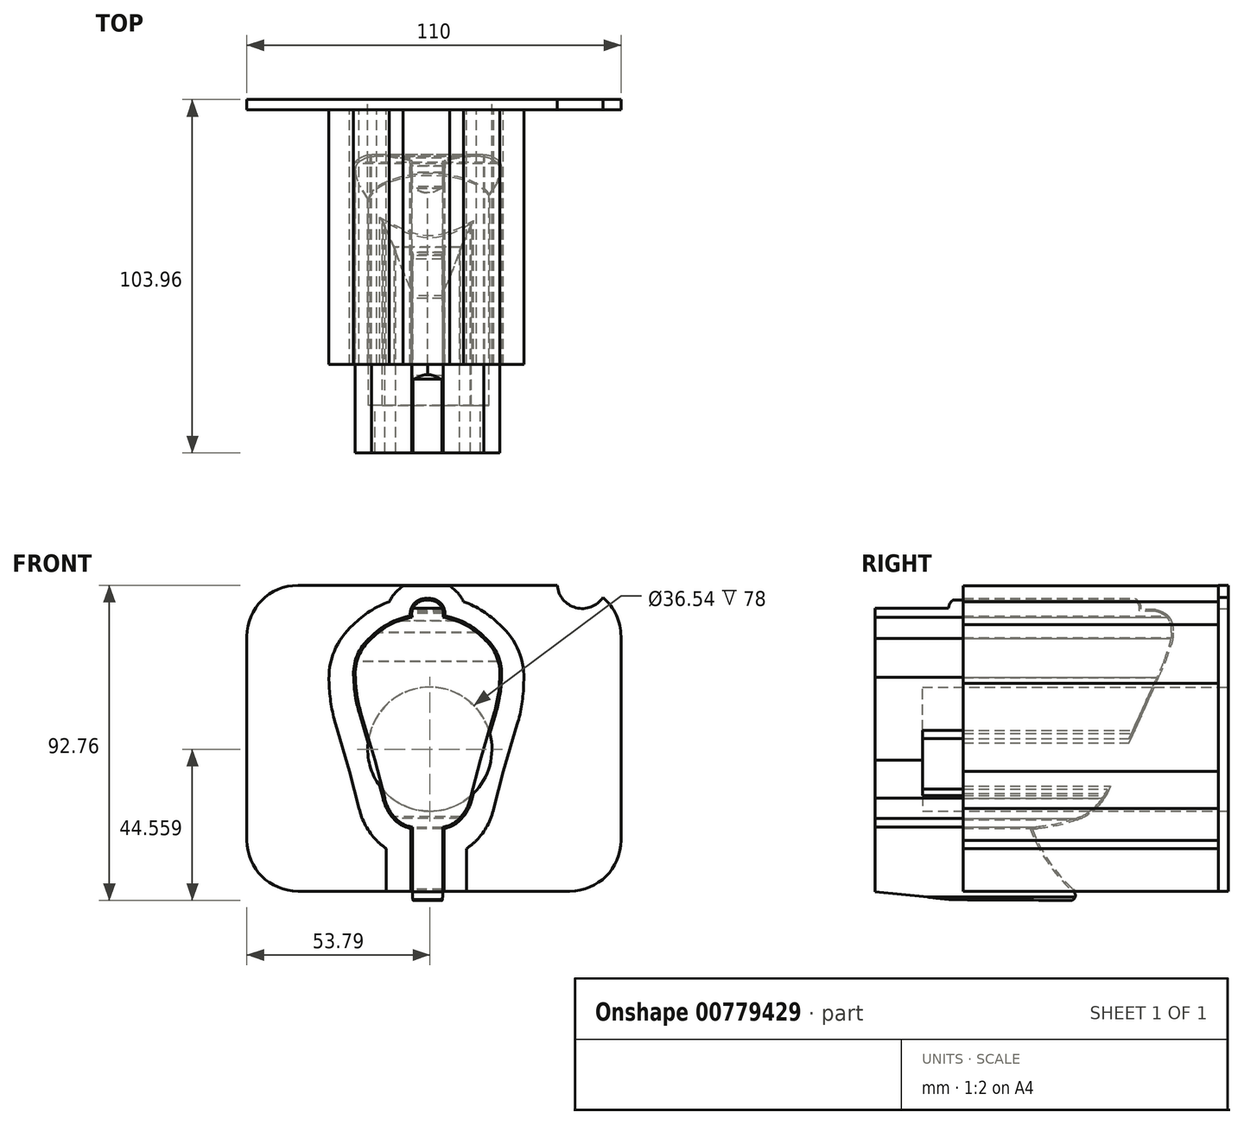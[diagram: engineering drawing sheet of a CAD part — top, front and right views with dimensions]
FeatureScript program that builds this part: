
annotation { "Feature Type Name" : "Feature", "Feature Type Description" : "" }
export const myFeature = defineFeature(function(context is Context, id is Id, definition is map)
    precondition{}
    {
        {
            var Q0;
            Q0=qCreatedBy(makeId("Front.planeOp"),FACE);
            var sketch = newSketch(context, id + "F0", { "sketchPlane" : qUnion([Q0])});
            skArc(sketch, "E0", {"start": v(0, -54.8) * mm, "mid": v(3.03, -53.66) * mm, "end": v(4.41, -50.73) * mm});
            skLineSegment(sketch, "E1", {"start": v(4.41, -50.73) * mm, "end": v(4.41, -30.1) * mm});
            skArc(sketch, "E2", {"start": v(4.41, -30.1) * mm, "mid": v(7.1, -29.25) * mm, "end": v(9.36, -27.55) * mm});
            skArc(sketch, "E3", {"start": v(9.36, -27.55) * mm, "mid": v(11.4, -24.8) * mm, "end": v(12.61, -21.6) * mm});
            skLineSegment(sketch, "E4", {"start": v(12.61, -21.6) * mm, "end": v(15.48, -10.44) * mm});
            skLineSegment(sketch, "E5", {"start": v(15.48, -10.44) * mm, "end": v(19.6, 3.52) * mm});
            skArc(sketch, "E6", {"start": v(16.49, 25.34) * mm, "mid": v(11, 29.45) * mm, "end": v(4.5, 31.58) * mm});
            skArc(sketch, "E7", {"start": v(4.5, 31.58) * mm, "mid": v(3.6, 35.3) * mm, "end": v(0, 36.62) * mm});
            skArc(sketch, "E8", {"start": v(19.6, 3.52) * mm, "mid": v(20.76, 8.66) * mm, "end": v(21.2, 13.91) * mm});
            skArc(sketch, "E9", {"start": v(21.2, 13.91) * mm, "mid": v(20.25, 20.2) * mm, "end": v(16.49, 25.34) * mm});
            skArc(sketch, "E10.MirrorCS", {"start": v(-4.5, 31.58) * mm, "mid": v(-3.6, 35.3) * mm, "end": v(0, 36.62) * mm});
            skArc(sketch, "E11.MirrorCS", {"start": v(-16.49, 25.34) * mm, "mid": v(-11, 29.45) * mm, "end": v(-4.5, 31.58) * mm});
            skArc(sketch, "E12.MirrorCS", {"start": v(-21.2, 13.91) * mm, "mid": v(-20.25, 20.2) * mm, "end": v(-16.49, 25.34) * mm});
            skArc(sketch, "E13.MirrorCS", {"start": v(-19.6, 3.52) * mm, "mid": v(-20.76, 8.66) * mm, "end": v(-21.2, 13.91) * mm});
            skLineSegment(sketch, "E14.MirrorCS", {"start": v(-15.48, -10.44) * mm, "end": v(-19.6, 3.52) * mm});
            skLineSegment(sketch, "E15.MirrorCS", {"start": v(-12.61, -21.6) * mm, "end": v(-15.48, -10.44) * mm});
            skArc(sketch, "E16.MirrorCS", {"start": v(-9.36, -27.55) * mm, "mid": v(-11.4, -24.8) * mm, "end": v(-12.61, -21.6) * mm});
            skLineSegment(sketch, "E17.MirrorCS", {"start": v(-4.41, -50.73) * mm, "end": v(-4.41, -30.1) * mm});
            skArc(sketch, "E18.MirrorCS", {"start": v(0, -54.8) * mm, "mid": v(-3.03, -53.66) * mm, "end": v(-4.41, -50.73) * mm});
            skArc(sketch, "E19.MirrorCS", {"start": v(-4.41, -30.1) * mm, "mid": v(-7.1, -29.25) * mm, "end": v(-9.36, -27.55) * mm});
            skSolve(sketch);
        }
        {
            var Q0;
            Q0=qCreatedBy(makeId("Right.planeOp"),FACE);
            var sketch = newSketch(context, id + "F1", { "sketchPlane" : qUnion([Q0])});
            skArc(sketch, "E20", {"start": v(13.07, -51.68) * mm, "mid": v(14.91, -50.75) * mm, "end": v(14.06, -48.88) * mm});
            skArc(sketch, "E21", {"start": v(1.55, -30.19) * mm, "mid": v(6.7, -40.27) * mm, "end": v(14.06, -48.88) * mm});
            skArc(sketch, "E22", {"start": v(1.55, -30.19) * mm, "mid": v(9.13, -29.26) * mm, "end": v(16.46, -27.11) * mm});
            skArc(sketch, "E23", {"start": v(16.46, -27.11) * mm, "mid": v(22.2, -22.57) * mm, "end": v(25.4, -15.99) * mm});
            skLineSegment(sketch, "E24", {"start": v(25.4, -15.99) * mm, "end": v(41.06, 18.67) * mm});
            skArc(sketch, "E25", {"start": v(33.8, 33.54) * mm, "mid": v(33.05, 36.18) * mm, "end": v(30.49, 37.18) * mm});
            skLineSegment(sketch, "E26", {"start": v(30.49, 37.18) * mm, "end": v(-19.33, 37.18) * mm});
            skArc(sketch, "E27", {"start": v(-19.33, 37.18) * mm, "mid": v(-21.39, 36.35) * mm, "end": v(-22.3, 34.33) * mm});
            skLineSegment(sketch, "E28", {"start": v(-22.3, 34.33) * mm, "end": v(-43.96, 34.33) * mm});
            skLineSegment(sketch, "E29", {"start": v(-43.96, 34.33) * mm, "end": v(-43.96, -49.1) * mm});
            skLineSegment(sketch, "E30", {"start": v(-43.96, -49.1) * mm, "end": v(-21.2, -51.48) * mm});
            skLineSegment(sketch, "E31", {"start": v(41.06, 18.67) * mm, "end": v(42.71, 23.65) * mm});
            skArc(sketch, "E32", {"start": v(42.71, 23.65) * mm, "mid": v(43.13, 25.36) * mm, "end": v(43.25, 27.12) * mm});
            skArc(sketch, "E33", {"start": v(43.25, 27.12) * mm, "mid": v(43.17, 28.82) * mm, "end": v(42.71, 30.46) * mm});
            skArc(sketch, "E34", {"start": v(42.71, 30.46) * mm, "mid": v(41.73, 31.86) * mm, "end": v(40.3, 32.8) * mm});
            skArc(sketch, "E35", {"start": v(40.3, 32.8) * mm, "mid": v(39.42, 33.14) * mm, "end": v(38.5, 33.37) * mm});
            skArc(sketch, "E36", {"start": v(33.8, 33.54) * mm, "mid": v(36.14, 33.42) * mm, "end": v(38.5, 33.37) * mm});
            skLineSegment(sketch, "E37", {"start": v(13.07, -51.68) * mm, "end": v(-21.2, -51.48) * mm});
            skSolve(sketch);
        }
        {
            var Q0;
            Q0 = qSketchRegion(id + "F0", true);
            extrude(context, id + "F2", {"entities" : qUnion([Q0]), "endBound" : BoundingType.SYMMETRIC, "depth" : 100 * mm, "offsetDistance" : 25 * mm});
        }
        {
            var Q0;
            Q0 = qSketchRegion(id + "F1", true);
            extrude(context, id + "F3", {"entities" : qUnion([Q0]), "endBound" : BoundingType.SYMMETRIC, "depth" : 50 * mm, "offsetDistance" : 25 * mm});
        }
        {
            var Q0;
            Q0=makeQuery(id+"F2.opExtrude","SWEPT_BODY",BODY,{"disambiguationData":[OSD([sQuery(id+"F0.wireOp",EDGE,"E0"),sQuery(id+"F0.wireOp",EDGE,"E1"),sQuery(id+"F0.wireOp",EDGE,"E3"),sQuery(id+"F0.wireOp",EDGE,"E4"),sQuery(id+"F0.wireOp",EDGE,"E5"),sQuery(id+"F0.wireOp",EDGE,"E6"),sQuery(id+"F0.wireOp",EDGE,"E7"),sQuery(id+"F0.wireOp",EDGE,"E8"),sQuery(id+"F0.wireOp",EDGE,"E9"),sQuery(id+"F0.wireOp",EDGE,"E10.MirrorCS"),sQuery(id+"F0.wireOp",EDGE,"E11.MirrorCS"),sQuery(id+"F0.wireOp",EDGE,"E12.MirrorCS"),sQuery(id+"F0.wireOp",EDGE,"E13.MirrorCS"),sQuery(id+"F0.wireOp",EDGE,"E14.MirrorCS"),sQuery(id+"F0.wireOp",EDGE,"E15.MirrorCS"),sQuery(id+"F0.wireOp",EDGE,"E16.MirrorCS"),sQuery(id+"F0.wireOp",EDGE,"E17.MirrorCS"),sQuery(id+"F0.wireOp",EDGE,"E18.MirrorCS"),sQuery(id+"F0.wireOp",EDGE,"E19.MirrorCS"),sQuery(id+"F0.wireOp",EDGE,"E2")])]});
            var Q1;
            Q1=makeQuery(id+"F3.opExtrude","SWEPT_BODY",BODY,{"disambiguationData":[OSD([sQuery(id+"F1.wireOp",EDGE,"dfYktmR6-UFK0-UMcN-eC6X-EMhfxDIhRWXA"),sQuery(id+"F1.wireOp",EDGE,"m5NG4yJs-mWs4-Z3ek-I9i2-yxJJIHfC6d3f"),sQuery(id+"F1.wireOp",EDGE,"E20"),sQuery(id+"F1.wireOp",EDGE,"E21"),sQuery(id+"F1.wireOp",EDGE,"E22"),sQuery(id+"F1.wireOp",EDGE,"E23"),sQuery(id+"F1.wireOp",EDGE,"E24"),sQuery(id+"F1.wireOp",EDGE,"E25"),sQuery(id+"F1.wireOp",EDGE,"E26"),sQuery(id+"F1.wireOp",EDGE,"E27"),sQuery(id+"F1.wireOp",EDGE,"E28"),sQuery(id+"F1.wireOp",EDGE,"E29"),sQuery(id+"F1.wireOp",EDGE,"E30"),sQuery(id+"F1.wireOp",EDGE,"E31"),sQuery(id+"F1.wireOp",EDGE,"E32"),sQuery(id+"F1.wireOp",EDGE,"E33"),sQuery(id+"F1.wireOp",EDGE,"E34"),sQuery(id+"F1.wireOp",EDGE,"E35"),sQuery(id+"F1.wireOp",EDGE,"E36")])]});
            booleanBodies(context, id + "F4", {"operationType" : BooleanOperationType.INTERSECTION, "tools" : qUnion([Q0, Q1])});
        }
        {
            var Q0;
            Q0=qCreatedBy(makeId("Front.planeOp"),FACE);
            var sketch = newSketch(context, id + "F5", { "sketchPlane" : qUnion([Q0])});
            skPoint(sketch, "E38.middle", {"position": v(0, 0) * mm});
            skLineSegment(sketch, "E39.bottom", {"start": v(-38.13, -39.18) * mm, "end": v(41.87, -39.18) * mm});
            skLineSegment(sketch, "E39.top", {"start": v(-38.13, 50.82) * mm, "end": v(38.14, 50.82) * mm});
            skLineSegment(sketch, "E39.left", {"start": v(-53.13, -24.18) * mm, "end": v(-53.13, 35.82) * mm});
            skLineSegment(sketch, "E39.right", {"start": v(56.87, -24.18) * mm, "end": v(56.87, 35.82) * mm});
            skPoint(sketch, "E40.visualSharp", {"position": v(-53.13, 50.82) * mm});
            skPoint(sketch, "E41.visualSharp", {"position": v(56.87, 50.82) * mm});
            skArc(sketch, "E41.filletArc", {"start": v(56.87, 35.82) * mm, "mid": v(55.49, 42.1) * mm, "end": v(51.6, 47.23) * mm});
            skPoint(sketch, "E42.visualSharp", {"position": v(56.87, -39.18) * mm});
            skArc(sketch, "E42.filletArc", {"start": v(41.87, -39.18) * mm, "mid": v(52.47, -34.79) * mm, "end": v(56.87, -24.18) * mm});
            skPoint(sketch, "E43.visualSharp", {"position": v(-53.13, -39.18) * mm});
            skArc(sketch, "E43.filletArc", {"start": v(-53.13, -24.18) * mm, "mid": v(-48.74, -34.79) * mm, "end": v(-38.13, -39.18) * mm});
            skArc(sketch, "E44.filletArc", {"start": v(-38.13, 50.82) * mm, "mid": v(-48.74, 46.42) * mm, "end": v(-53.13, 35.82) * mm});
            skArc(sketch, "E45", {"start": v(38.14, 50.82) * mm, "mid": v(43.6, 44.25) * mm, "end": v(51.6, 47.23) * mm});
            skCircle(sketch, "E46", {"center": v(0.66, 2.62) * mm, "radius": 18.27 * mm});
            skPoint(sketch, "E46.first.point", {"position": v(-11.43, -11.08) * mm});
            skPoint(sketch, "E46.second.point", {"position": v(12.85, 16.23) * mm});
            skPoint(sketch, "E46.third.point", {"position": v(17.46, -4.55) * mm});
            skSolve(sketch);
        }
        {
            var Q0;
            Q0=makeQuery(id+"F4.opBoolean","INTERSECT",BODY,{"derivedFrom":[makeQuery(id+"F2.opExtrude","SWEPT_BODY",BODY,{"disambiguationData":[OSD([sQuery(id+"F0.wireOp",EDGE,"E0"),sQuery(id+"F0.wireOp",EDGE,"E1"),sQuery(id+"F0.wireOp",EDGE,"E3"),sQuery(id+"F0.wireOp",EDGE,"E4"),sQuery(id+"F0.wireOp",EDGE,"E5"),sQuery(id+"F0.wireOp",EDGE,"E6"),sQuery(id+"F0.wireOp",EDGE,"E7"),sQuery(id+"F0.wireOp",EDGE,"E8"),sQuery(id+"F0.wireOp",EDGE,"E9"),sQuery(id+"F0.wireOp",EDGE,"E10.MirrorCS"),sQuery(id+"F0.wireOp",EDGE,"E11.MirrorCS"),sQuery(id+"F0.wireOp",EDGE,"E12.MirrorCS"),sQuery(id+"F0.wireOp",EDGE,"E13.MirrorCS"),sQuery(id+"F0.wireOp",EDGE,"E14.MirrorCS"),sQuery(id+"F0.wireOp",EDGE,"E15.MirrorCS"),sQuery(id+"F0.wireOp",EDGE,"E16.MirrorCS"),sQuery(id+"F0.wireOp",EDGE,"E17.MirrorCS"),sQuery(id+"F0.wireOp",EDGE,"E18.MirrorCS"),sQuery(id+"F0.wireOp",EDGE,"E19.MirrorCS"),sQuery(id+"F0.wireOp",EDGE,"E2")])]}),makeQuery(id+"F3.opExtrude","SWEPT_BODY",BODY,{"disambiguationData":[OSD([sQuery(id+"F1.wireOp",EDGE,"dfYktmR6-UFK0-UMcN-eC6X-EMhfxDIhRWXA"),sQuery(id+"F1.wireOp",EDGE,"m5NG4yJs-mWs4-Z3ek-I9i2-yxJJIHfC6d3f"),sQuery(id+"F1.wireOp",EDGE,"E20"),sQuery(id+"F1.wireOp",EDGE,"E21"),sQuery(id+"F1.wireOp",EDGE,"E22"),sQuery(id+"F1.wireOp",EDGE,"E23"),sQuery(id+"F1.wireOp",EDGE,"E24"),sQuery(id+"F1.wireOp",EDGE,"E25"),sQuery(id+"F1.wireOp",EDGE,"E26"),sQuery(id+"F1.wireOp",EDGE,"E27"),sQuery(id+"F1.wireOp",EDGE,"E28"),sQuery(id+"F1.wireOp",EDGE,"E29"),sQuery(id+"F1.wireOp",EDGE,"E30"),sQuery(id+"F1.wireOp",EDGE,"E31"),sQuery(id+"F1.wireOp",EDGE,"E32"),sQuery(id+"F1.wireOp",EDGE,"E33"),sQuery(id+"F1.wireOp",EDGE,"E34"),sQuery(id+"F1.wireOp",EDGE,"E35"),sQuery(id+"F1.wireOp",EDGE,"E36")])]})]});
            transform(context, id + "F6", {"entities" : qUnion([Q0]), "transformType" : TransformType.TRANSLATION_3D, "dx" : 0 * mm, "dy" : -70 * mm, "dz" : 9.8 * mm, "makeCopy" : false});
        }
        {
            var Q0;
            Q0=qCreatedBy(makeId("Front.planeOp"),FACE);
            var sketch = newSketch(context, id + "F7", { "sketchPlane" : qUnion([Q0])});
            skArc(sketch, "E47.0", {"start": v(-27.03, 9.89) * mm, "mid": v(-28.38, 15.88) * mm, "end": v(-28.94, 22) * mm});
            skLineSegment(sketch, "E47.1", {"start": v(-22.95, -3.95) * mm, "end": v(-27.03, 9.89) * mm});
            skLineSegment(sketch, "E47.2", {"start": v(-20.14, -14.87) * mm, "end": v(-22.95, -3.95) * mm});
            skArc(sketch, "E47.3", {"start": v(-15.03, -24.23) * mm, "mid": v(-18.23, -19.9) * mm, "end": v(-20.14, -14.87) * mm});
            skArc(sketch, "E47.4", {"start": v(-12.14, -26.61) * mm, "mid": v(-13.66, -25.5) * mm, "end": v(-15.03, -24.23) * mm});
            skArc(sketch, "E47.5", {"start": v(-28.94, 22) * mm, "mid": v(-27.45, 31.44) * mm, "end": v(-21.89, 39.21) * mm});
            skLineSegment(sketch, "E47.6", {"start": v(-12.14, -39.18) * mm, "end": v(-12.14, -26.61) * mm});
            skLineSegment(sketch, "E47.9", {"start": v(11.48, -39.18) * mm, "end": v(11.48, -26.6) * mm});
            skArc(sketch, "E47.10", {"start": v(21.22, 39.22) * mm, "mid": v(16.28, 43.22) * mm, "end": v(10.58, 46.02) * mm});
            skArc(sketch, "E47.11", {"start": v(10.58, 46.02) * mm, "mid": v(8.86, 48.63) * mm, "end": v(6.5, 50.68) * mm});
            skArc(sketch, "E47.12", {"start": v(-11.25, 46) * mm, "mid": v(-9.52, 48.63) * mm, "end": v(-7.15, 50.68) * mm});
            skArc(sketch, "E47.13", {"start": v(-21.89, 39.21) * mm, "mid": v(-16.95, 43.2) * mm, "end": v(-11.25, 46) * mm});
            skArc(sketch, "E47.14", {"start": v(28.27, 22) * mm, "mid": v(26.79, 31.45) * mm, "end": v(21.22, 39.22) * mm});
            skArc(sketch, "E47.15", {"start": v(26.37, 9.9) * mm, "mid": v(27.72, 15.88) * mm, "end": v(28.27, 22) * mm});
            skLineSegment(sketch, "E47.16", {"start": v(22.29, -3.94) * mm, "end": v(26.37, 9.9) * mm});
            skLineSegment(sketch, "E47.17", {"start": v(19.47, -14.86) * mm, "end": v(22.29, -3.94) * mm});
            skArc(sketch, "E47.18", {"start": v(14.36, -24.22) * mm, "mid": v(17.56, -19.9) * mm, "end": v(19.47, -14.86) * mm});
            skArc(sketch, "E47.19", {"start": v(11.48, -26.6) * mm, "mid": v(13, -25.5) * mm, "end": v(14.36, -24.22) * mm});
            skLineSegment(sketch, "E48", {"start": v(-12.14, -39.18) * mm, "end": v(11.48, -39.18) * mm});
            skLineSegment(sketch, "E49", {"start": v(-7.15, 50.68) * mm, "end": v(6.5, 50.68) * mm});
            skSolve(sketch);
        }
        {
            var Q0;
            Q0 = qSketchRegion(id + "F7", true);
            extrude(context, id + "F8", {"entities" : qUnion([Q0]), "depth" : 78 * mm, "offsetDistance" : 25 * mm});
        }
        {
            var Q0;
            Q0 = qSketchRegion(id + "F5", true);
            extrude(context, id + "F9", {"entities" : qUnion([Q0]), "operationType" : NewBodyOperationType.ADD, "depth" : 3 * mm, "offsetDistance" : 25 * mm});
        }
        {
            var Q0;
            Q0=makeQuery(id+"F5.imprint","IMPRINT",FACE,{"disambiguationData":[TD([[makeQuery(id+"F5.imprint","IMPRINT",EDGE,{"derivedFrom":sQuery(id+"F5.wireOp",EDGE,"E46")}),1.0]])]});
            var Q1;
            Q1=sQuery(id+"F5.wireOp",EDGE,"E46");
            extrude(context, id + "F10", {"entities" : qUnion([Q0]), "operationType" : NewBodyOperationType.REMOVE, "surfaceEntities" : qUnion([Q1]), "depth" : 100 * mm, "offsetDistance" : 25 * mm});
        }
        {
            var Q0;
            Q0=makeQuery(id+"F4.opBoolean","INTERSECT",BODY,{"derivedFrom":[makeQuery(id+"F2.opExtrude","SWEPT_BODY",BODY,{"disambiguationData":[OSD([sQuery(id+"F0.wireOp",EDGE,"E0"),sQuery(id+"F0.wireOp",EDGE,"E1"),sQuery(id+"F0.wireOp",EDGE,"E3"),sQuery(id+"F0.wireOp",EDGE,"E4"),sQuery(id+"F0.wireOp",EDGE,"E5"),sQuery(id+"F0.wireOp",EDGE,"E6"),sQuery(id+"F0.wireOp",EDGE,"E7"),sQuery(id+"F0.wireOp",EDGE,"E8"),sQuery(id+"F0.wireOp",EDGE,"E9"),sQuery(id+"F0.wireOp",EDGE,"E10.MirrorCS"),sQuery(id+"F0.wireOp",EDGE,"E11.MirrorCS"),sQuery(id+"F0.wireOp",EDGE,"E12.MirrorCS"),sQuery(id+"F0.wireOp",EDGE,"E13.MirrorCS"),sQuery(id+"F0.wireOp",EDGE,"E14.MirrorCS"),sQuery(id+"F0.wireOp",EDGE,"E15.MirrorCS"),sQuery(id+"F0.wireOp",EDGE,"E16.MirrorCS"),sQuery(id+"F0.wireOp",EDGE,"E17.MirrorCS"),sQuery(id+"F0.wireOp",EDGE,"E18.MirrorCS"),sQuery(id+"F0.wireOp",EDGE,"E19.MirrorCS"),sQuery(id+"F0.wireOp",EDGE,"E2")])]}),makeQuery(id+"F3.opExtrude","SWEPT_BODY",BODY,{"disambiguationData":[OSD([sQuery(id+"F1.wireOp",EDGE,"dfYktmR6-UFK0-UMcN-eC6X-EMhfxDIhRWXA"),sQuery(id+"F1.wireOp",EDGE,"m5NG4yJs-mWs4-Z3ek-I9i2-yxJJIHfC6d3f"),sQuery(id+"F1.wireOp",EDGE,"E20"),sQuery(id+"F1.wireOp",EDGE,"E21"),sQuery(id+"F1.wireOp",EDGE,"E22"),sQuery(id+"F1.wireOp",EDGE,"E23"),sQuery(id+"F1.wireOp",EDGE,"E24"),sQuery(id+"F1.wireOp",EDGE,"E25"),sQuery(id+"F1.wireOp",EDGE,"E26"),sQuery(id+"F1.wireOp",EDGE,"E27"),sQuery(id+"F1.wireOp",EDGE,"E28"),sQuery(id+"F1.wireOp",EDGE,"E29"),sQuery(id+"F1.wireOp",EDGE,"E30"),sQuery(id+"F1.wireOp",EDGE,"E31"),sQuery(id+"F1.wireOp",EDGE,"E32"),sQuery(id+"F1.wireOp",EDGE,"E33"),sQuery(id+"F1.wireOp",EDGE,"E34"),sQuery(id+"F1.wireOp",EDGE,"E35"),sQuery(id+"F1.wireOp",EDGE,"E36")])]})]});
            transform(context, id + "F11", {"entities" : qUnion([Q0]), "transformType" : TransformType.TRANSLATION_3D, "dx" : 0 * mm, "dy" : 10 * mm, "dz" : 0 * mm, "makeCopy" : false});
        }
        {
            var Q0;
            Q0=makeQuery(id+"F4.opBoolean","INTERSECT",BODY,{"derivedFrom":[makeQuery(id+"F2.opExtrude","SWEPT_BODY",BODY,{"disambiguationData":[OSD([sQuery(id+"F0.wireOp",EDGE,"E0"),sQuery(id+"F0.wireOp",EDGE,"E1"),sQuery(id+"F0.wireOp",EDGE,"E3"),sQuery(id+"F0.wireOp",EDGE,"E4"),sQuery(id+"F0.wireOp",EDGE,"E5"),sQuery(id+"F0.wireOp",EDGE,"E6"),sQuery(id+"F0.wireOp",EDGE,"E7"),sQuery(id+"F0.wireOp",EDGE,"E8"),sQuery(id+"F0.wireOp",EDGE,"E9"),sQuery(id+"F0.wireOp",EDGE,"E10.MirrorCS"),sQuery(id+"F0.wireOp",EDGE,"E11.MirrorCS"),sQuery(id+"F0.wireOp",EDGE,"E12.MirrorCS"),sQuery(id+"F0.wireOp",EDGE,"E13.MirrorCS"),sQuery(id+"F0.wireOp",EDGE,"E14.MirrorCS"),sQuery(id+"F0.wireOp",EDGE,"E15.MirrorCS"),sQuery(id+"F0.wireOp",EDGE,"E16.MirrorCS"),sQuery(id+"F0.wireOp",EDGE,"E17.MirrorCS"),sQuery(id+"F0.wireOp",EDGE,"E18.MirrorCS"),sQuery(id+"F0.wireOp",EDGE,"E19.MirrorCS"),sQuery(id+"F0.wireOp",EDGE,"E2")])]}),makeQuery(id+"F3.opExtrude","SWEPT_BODY",BODY,{"disambiguationData":[OSD([sQuery(id+"F1.wireOp",EDGE,"dfYktmR6-UFK0-UMcN-eC6X-EMhfxDIhRWXA"),sQuery(id+"F1.wireOp",EDGE,"m5NG4yJs-mWs4-Z3ek-I9i2-yxJJIHfC6d3f"),sQuery(id+"F1.wireOp",EDGE,"E20"),sQuery(id+"F1.wireOp",EDGE,"E21"),sQuery(id+"F1.wireOp",EDGE,"E22"),sQuery(id+"F1.wireOp",EDGE,"E23"),sQuery(id+"F1.wireOp",EDGE,"E24"),sQuery(id+"F1.wireOp",EDGE,"E25"),sQuery(id+"F1.wireOp",EDGE,"E26"),sQuery(id+"F1.wireOp",EDGE,"E27"),sQuery(id+"F1.wireOp",EDGE,"E28"),sQuery(id+"F1.wireOp",EDGE,"E29"),sQuery(id+"F1.wireOp",EDGE,"E30"),sQuery(id+"F1.wireOp",EDGE,"E31"),sQuery(id+"F1.wireOp",EDGE,"E32"),sQuery(id+"F1.wireOp",EDGE,"E33"),sQuery(id+"F1.wireOp",EDGE,"E34"),sQuery(id+"F1.wireOp",EDGE,"E35"),sQuery(id+"F1.wireOp",EDGE,"E36")])]})]});
            var Q1;
            Q1=makeQuery(id+"F8.opExtrude","SWEPT_BODY",BODY,{"disambiguationData":[OSD([sQuery(id+"F7.wireOp",EDGE,"E47.0"),sQuery(id+"F7.wireOp",EDGE,"E47.1"),sQuery(id+"F7.wireOp",EDGE,"E47.2"),sQuery(id+"F7.wireOp",EDGE,"E47.3"),sQuery(id+"F7.wireOp",EDGE,"E47.4"),sQuery(id+"F7.wireOp",EDGE,"E47.5"),sQuery(id+"F7.wireOp",EDGE,"E47.6"),sQuery(id+"F7.wireOp",EDGE,"E47.9"),sQuery(id+"F7.wireOp",EDGE,"E47.10"),sQuery(id+"F7.wireOp",EDGE,"E47.11"),sQuery(id+"F7.wireOp",EDGE,"E47.12"),sQuery(id+"F7.wireOp",EDGE,"E47.13"),sQuery(id+"F7.wireOp",EDGE,"E47.14"),sQuery(id+"F7.wireOp",EDGE,"E47.15"),sQuery(id+"F7.wireOp",EDGE,"E47.16"),sQuery(id+"F7.wireOp",EDGE,"E47.17"),sQuery(id+"F7.wireOp",EDGE,"E47.18"),sQuery(id+"F7.wireOp",EDGE,"E47.19"),sQuery(id+"F7.wireOp",EDGE,"E48"),sQuery(id+"F7.wireOp",EDGE,"E49")])]});
            var Q2;
            Q2=makeQuery(id+"F2.opExtrude","SWEPT_FACE",FACE,{"disambiguationData":[OSD([sQuery(id+"F0.wireOp",EDGE,"E7")])]});
            var Q3;
            Q3=makeQuery(id+"F2.opExtrude","SWEPT_FACE",FACE,{"disambiguationData":[OSD([sQuery(id+"F0.wireOp",EDGE,"E6")])]});
            var Q4;
            Q4=makeQuery(id+"F2.opExtrude","SWEPT_FACE",FACE,{"disambiguationData":[OSD([sQuery(id+"F0.wireOp",EDGE,"E9")])]});
            var Q5;
            Q5=makeQuery(id+"F2.opExtrude","SWEPT_FACE",FACE,{"disambiguationData":[OSD([sQuery(id+"F0.wireOp",EDGE,"E8")])]});
            var Q6;
            Q6=makeQuery(id+"F2.opExtrude","SWEPT_FACE",FACE,{"disambiguationData":[OSD([sQuery(id+"F0.wireOp",EDGE,"E5")])]});
            var Q7;
            Q7=makeQuery(id+"F2.opExtrude","SWEPT_FACE",FACE,{"disambiguationData":[OSD([sQuery(id+"F0.wireOp",EDGE,"E4")])]});
            var Q8;
            Q8=makeQuery(id+"F2.opExtrude","SWEPT_FACE",FACE,{"disambiguationData":[OSD([sQuery(id+"F0.wireOp",EDGE,"E2")])]});
            var Q9;
            Q9=makeQuery(id+"F2.opExtrude","SWEPT_FACE",FACE,{"disambiguationData":[OSD([sQuery(id+"F0.wireOp",EDGE,"E3")])]});
            var Q10;
            Q10=makeQuery(id+"F2.opExtrude","SWEPT_FACE",FACE,{"disambiguationData":[OSD([sQuery(id+"F0.wireOp",EDGE,"E1")])]});
            var Q11;
            Q11=makeQuery(id+"F2.opExtrude","SWEPT_FACE",FACE,{"disambiguationData":[OSD([sQuery(id+"F0.wireOp",EDGE,"E10.MirrorCS")])]});
            var Q12;
            Q12=makeQuery(id+"F2.opExtrude","SWEPT_FACE",FACE,{"disambiguationData":[OSD([sQuery(id+"F0.wireOp",EDGE,"E11.MirrorCS")])]});
            var Q13;
            Q13=makeQuery(id+"F2.opExtrude","SWEPT_FACE",FACE,{"disambiguationData":[OSD([sQuery(id+"F0.wireOp",EDGE,"E12.MirrorCS")])]});
            var Q14;
            Q14=makeQuery(id+"F2.opExtrude","SWEPT_FACE",FACE,{"disambiguationData":[OSD([sQuery(id+"F0.wireOp",EDGE,"E13.MirrorCS")])]});
            var Q15;
            Q15=makeQuery(id+"F2.opExtrude","SWEPT_FACE",FACE,{"disambiguationData":[OSD([sQuery(id+"F0.wireOp",EDGE,"E14.MirrorCS")])]});
            var Q16;
            Q16=makeQuery(id+"F2.opExtrude","SWEPT_FACE",FACE,{"disambiguationData":[OSD([sQuery(id+"F0.wireOp",EDGE,"E15.MirrorCS")])]});
            var Q17;
            Q17=makeQuery(id+"F2.opExtrude","SWEPT_FACE",FACE,{"disambiguationData":[OSD([sQuery(id+"F0.wireOp",EDGE,"E16.MirrorCS")])]});
            var Q18;
            Q18=makeQuery(id+"F2.opExtrude","SWEPT_FACE",FACE,{"disambiguationData":[OSD([sQuery(id+"F0.wireOp",EDGE,"E17.MirrorCS")])]});
            var Q19;
            Q19=makeQuery(id+"F2.opExtrude","SWEPT_FACE",FACE,{"disambiguationData":[OSD([sQuery(id+"F0.wireOp",EDGE,"E19.MirrorCS")])]});
            var Q20;
            Q20=makeQuery(id+"F3.opExtrude","SWEPT_FACE",FACE,{"disambiguationData":[OSD([sQuery(id+"F1.wireOp",EDGE,"E25")])]});
            var Q21;
            Q21=makeQuery(id+"F3.opExtrude","SWEPT_FACE",FACE,{"disambiguationData":[OSD([sQuery(id+"F1.wireOp",EDGE,"E36")])]});
            var Q22;
            Q22=makeQuery(id+"F3.opExtrude","SWEPT_FACE",FACE,{"disambiguationData":[OSD([sQuery(id+"F1.wireOp",EDGE,"E34")])]});
            var Q23;
            Q23=makeQuery(id+"F3.opExtrude","SWEPT_FACE",FACE,{"disambiguationData":[OSD([sQuery(id+"F1.wireOp",EDGE,"E35")])]});
            var Q24;
            Q24=makeQuery(id+"F3.opExtrude","SWEPT_FACE",FACE,{"disambiguationData":[OSD([sQuery(id+"F1.wireOp",EDGE,"E33")])]});
            var Q25;
            Q25=makeQuery(id+"F3.opExtrude","SWEPT_FACE",FACE,{"disambiguationData":[OSD([sQuery(id+"F1.wireOp",EDGE,"E32")])]});
            var Q26;
            Q26=makeQuery(id+"F3.opExtrude","SWEPT_FACE",FACE,{"disambiguationData":[OSD([sQuery(id+"F1.wireOp",EDGE,"E31")])]});
            var Q27;
            Q27=makeQuery(id+"F3.opExtrude","SWEPT_FACE",FACE,{"disambiguationData":[OSD([sQuery(id+"F1.wireOp",EDGE,"E24")])]});
            var Q28;
            Q28=makeQuery(id+"F3.opExtrude","SWEPT_FACE",FACE,{"disambiguationData":[OSD([sQuery(id+"F1.wireOp",EDGE,"E22")])]});
            var Q29;
            Q29=makeQuery(id+"F3.opExtrude","SWEPT_FACE",FACE,{"disambiguationData":[OSD([sQuery(id+"F1.wireOp",EDGE,"E23")])]});
            var Q30;
            Q30=makeQuery(id+"F3.opExtrude","SWEPT_FACE",FACE,{"disambiguationData":[OSD([sQuery(id+"F1.wireOp",EDGE,"E21")])]});
            var Q31;
            Q31=makeQuery(id+"F3.opExtrude","SWEPT_FACE",FACE,{"disambiguationData":[OSD([sQuery(id+"F1.wireOp",EDGE,"E20")])]});
            var Q32;
            Q32=makeQuery(id+"F3.opExtrude","SWEPT_FACE",FACE,{"disambiguationData":[OSD([sQuery(id+"F1.wireOp",EDGE,"m5NG4yJs-mWs4-Z3ek-I9i2-yxJJIHfC6d3f")])]});
            booleanBodies(context, id + "F12", {"operationType" : BooleanOperationType.SUBTRACTION, "tools" : qUnion([Q0]), "targets" : qUnion([Q1]), "offset" : true, "offsetAll" : true, "entitiesToOffset" : qUnion([Q2, Q3, Q4, Q5, Q6, Q7, Q8, Q9, Q10, Q11, Q12, Q13, Q14, Q15, Q16, Q17, Q18, Q19, Q20, Q21, Q22, Q23, Q24, Q25, Q26, Q27, Q28, Q29, Q30, Q31, Q32]), "offsetDistance" : 0.5 * mm, "keepTools" : true});
        }
    });
